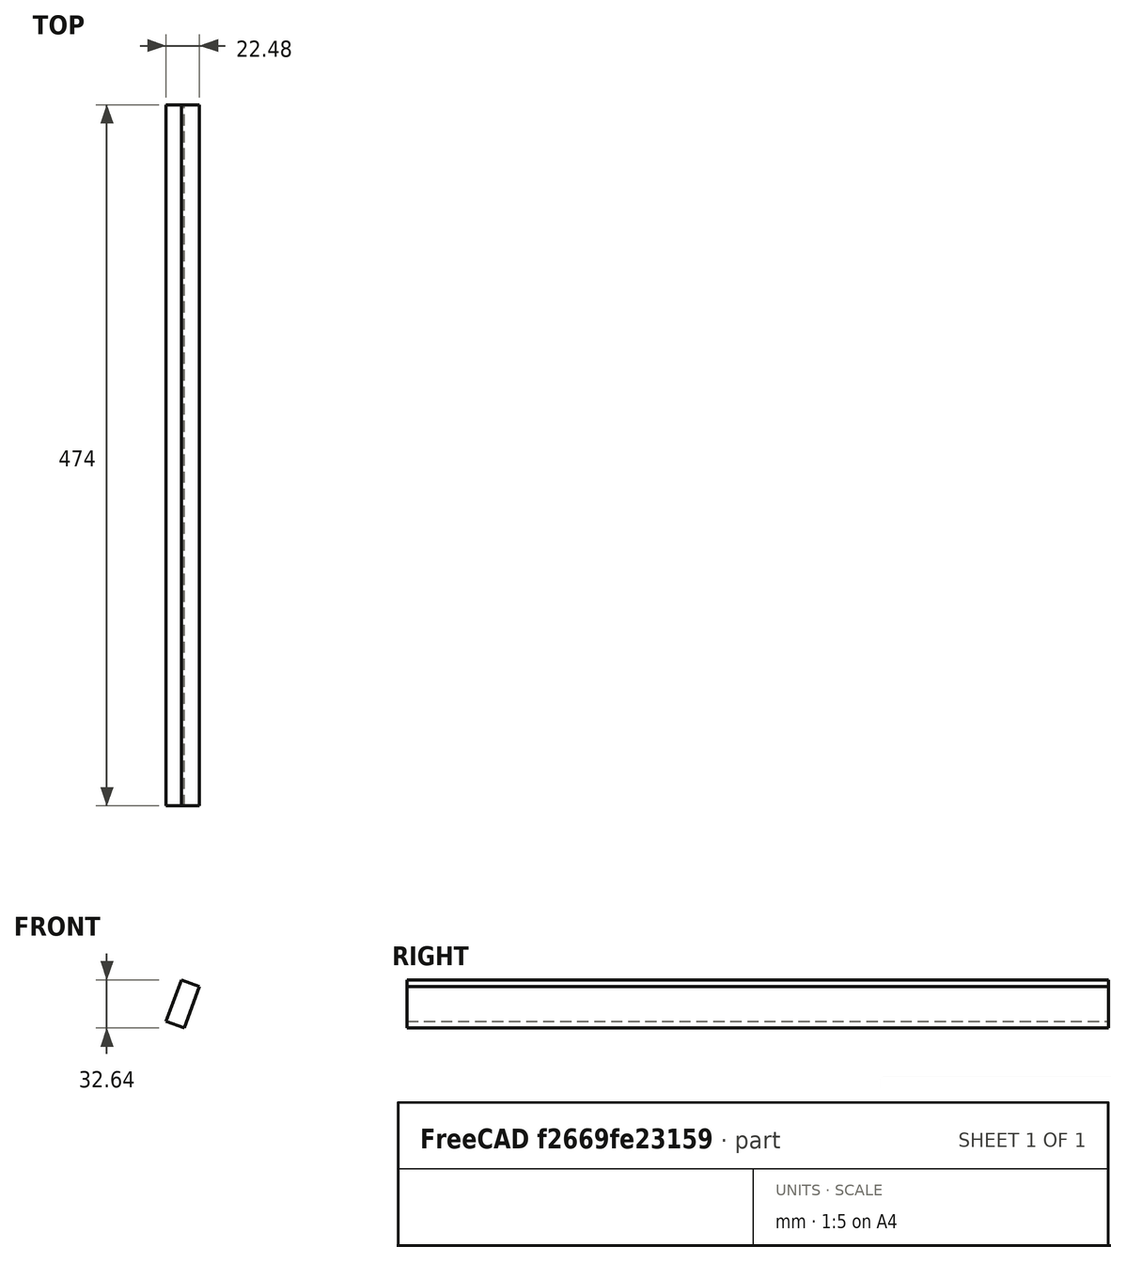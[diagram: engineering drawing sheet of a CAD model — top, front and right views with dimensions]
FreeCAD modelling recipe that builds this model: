
FCSTD DOCUMENT  (FreeCAD 0.18R14555 (Git shallow))
Label: 4000_Body_front_YZ
License: All rights reserved
LicenseURL: http://en.wikipedia.org/wiki/All_rights_reserved
objects: Spreadsheet::Sheet×1, Sketcher::SketchObject×1, PartDesign::Pad×1, PartDesign::Body×1
note: 4 computed .brp shape members not serialized (recipe doc carries the construction recipe); baked Part::Feature solids carry a one-line shape summary decoded from their .brp

FEATURE [Spreadsheet::Sheet] Spreadsheet  label="xls"
  cells = B5=BODY FRONT; E5=nominal size; B6=Board Thickness; C6(thickness)=13; D6=xls.thickness; B7=Horizontal Y; C7(width)==+E7 - 2 * C6; D7=xls.width; E7=500; B8=X=; C8(height)=30; D8=xls.height; B9=Angle Y; C9(tilt)=70; D9=xls.tilt
FEATURE [Sketcher::SketchObject] Sketch
  MapMode = 5
  Placement = pos=(0,0,0) rot=(1,0,0;1.5708rad)
  Support = -> [XZ_Plane]
  expr: Constraints[8] = xls.tilt
  expr: Constraints[7] = xls.height
  expr: Constraints[6] = xls.thickness
  sketch-geometry (4):
    g0: LineSegment StartX=12.216 StartY=-4.44626 StartZ=0 EndX=22.4766 EndY=23.7445 EndZ=0
    g1: LineSegment StartX=22.4766 StartY=23.7445 StartZ=0 EndX=10.2606 EndY=28.1908 EndZ=0
    g2: LineSegment StartX=10.2606 StartY=28.1908 StartZ=0 EndX=0 EndY=0 EndZ=0
    g3: LineSegment StartX=0 StartY=0 StartZ=0 EndX=12.216 EndY=-4.44626 EndZ=0
  constraints (11):
    c: Coincident(g0,g1)
    c: Coincident(g1,g2)
    c: Coincident(g2,g3)
    c: Parallel(g3,g1)
    c: Parallel(g0,g2)
    c: Perpendicular(g0,g3)
    c: Distance(g3) = 13
    c: Distance(g0) = 30
    c: Angle(g-1,g0) = 1.22173
    c: Coincident(g0,g3)
    c: Coincident(g-1,g2)
FEATURE [PartDesign::Pad] Pad
  Length = 474
  Length2 = 100
  Placement = pos=(0,0,0) rot=(1,0,0;1.5708rad)
  Profile = -> Sketch
  Reversed = true
  Type = 0
  expr: Length = xls.width
FEATURE [PartDesign::Body] Body
  Group = -> [Sketch,Pad]
  Origin = -> Origin
  Tip = -> Pad
